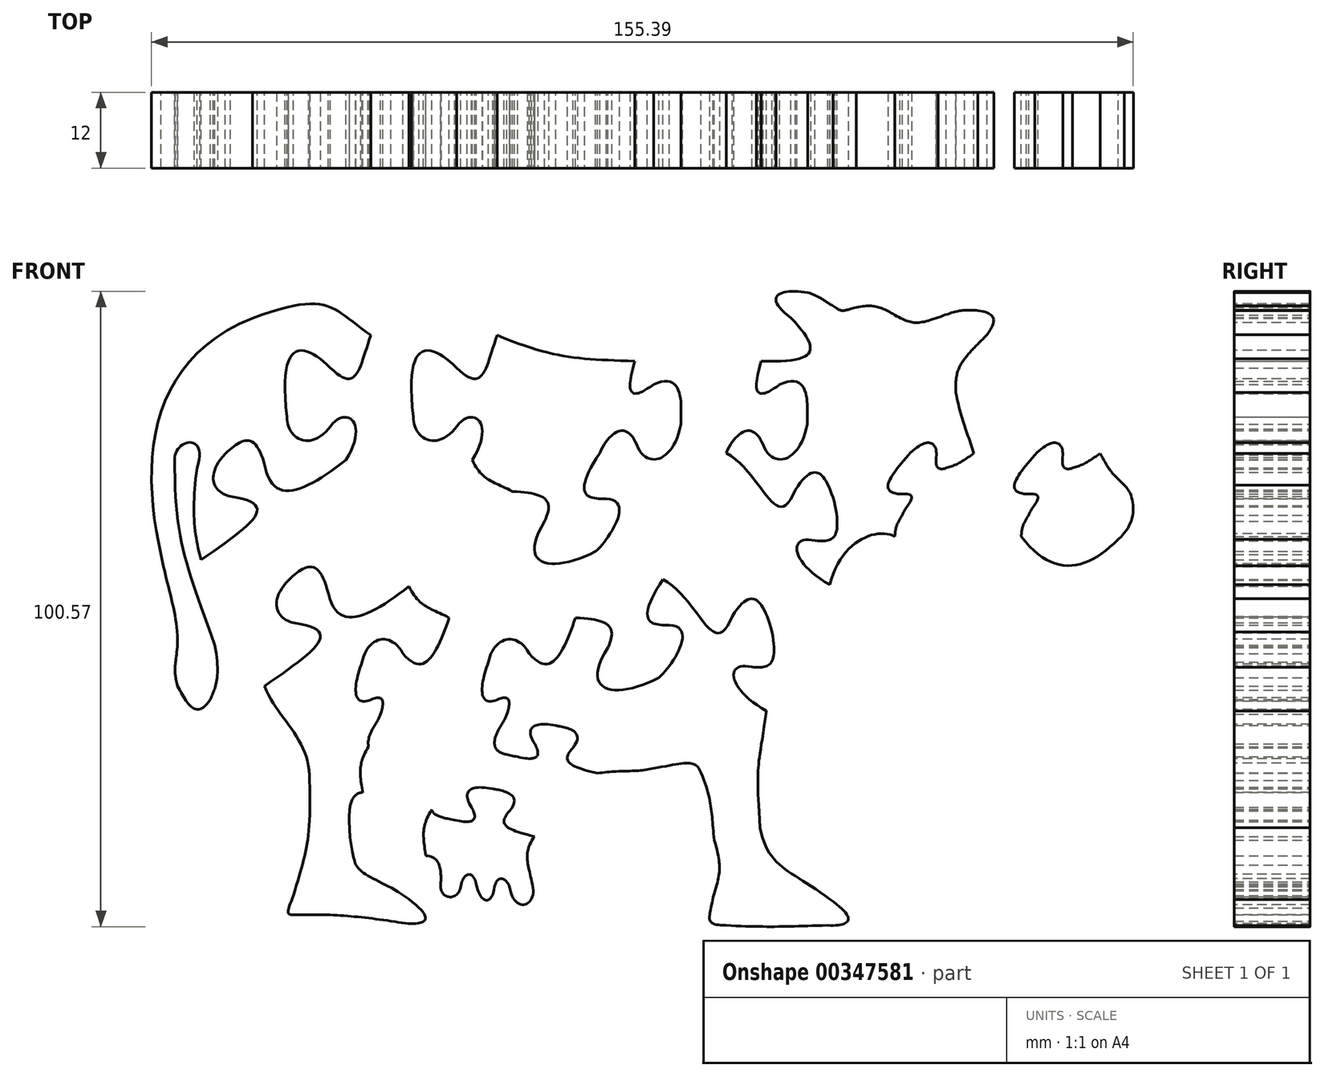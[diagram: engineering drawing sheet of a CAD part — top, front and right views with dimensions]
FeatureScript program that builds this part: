
annotation { "Feature Type Name" : "Feature", "Feature Type Description" : "" }
export const myFeature = defineFeature(function(context is Context, id is Id, definition is map)
    precondition{}
    {
        {
            var Q0;
            Q0=qCreatedBy(makeId("Front.planeOp"),FACE);
            var sketch = newSketch(context, id + "F0", { "sketchPlane" : qUnion([Q0])});
            skFitSpline(sketch, "E0", {"points": [v(-32.6, 40.87) * mm, v(-13.83, 38.18) * mm], "startDerivative": vector(36.75, 13.6) * mm, "endDerivative": vector(18.9, -13.17) * mm});
            skFitSpline(sketch, "E1", {"points": [v(-13.83, 38.18) * mm, v(7.96, 34.07) * mm], "startDerivative": vector(27.03, -11.28) * mm, "endDerivative": vector(27.04, -1.05) * mm});
            skFitSpline(sketch, "E2", {"points": [v(7.96, 34.07) * mm, v(12.64, 40.93) * mm], "startDerivative": vector(26.9, -0.75) * mm, "endDerivative": vector(-14.95, 15.64) * mm});
            skFitSpline(sketch, "E3", {"points": [v(12.64, 40.93) * mm, v(15.32, 44.94) * mm], "startDerivative": vector(-14.2, 10.76) * mm, "endDerivative": vector(12.86, -2.14) * mm});
            skFitSpline(sketch, "E4", {"points": [v(15.32, 44.94) * mm, v(19.28, 42.85) * mm], "startDerivative": vector(6.61, -2.14) * mm, "endDerivative": vector(3.96, -2.08) * mm});
            skFitSpline(sketch, "E5", {"points": [v(19.28, 42.85) * mm, v(22.97, 42.59) * mm], "startDerivative": vector(5.1, -3.48) * mm, "endDerivative": vector(6.7, 1.6) * mm});
            skFitSpline(sketch, "E6", {"points": [v(22.97, 42.59) * mm, v(29.1, 41.4) * mm], "startDerivative": vector(8.42, 1.81) * mm, "endDerivative": vector(6.88, -3.85) * mm});
            skFitSpline(sketch, "E7", {"points": [v(29.1, 41.4) * mm, v(35.97, 41) * mm], "startDerivative": vector(7.85, -4.56) * mm, "endDerivative": vector(10.17, 3.54) * mm});
            skFitSpline(sketch, "E8", {"points": [v(35.97, 41) * mm, v(42.23, 42.1) * mm], "startDerivative": vector(9.41, 3.73) * mm, "endDerivative": vector(6.05, -0.42) * mm});
            skFitSpline(sketch, "E9", {"points": [v(42.23, 42.1) * mm, v(43.66, 38.26) * mm], "startDerivative": vector(10.46, -1.27) * mm, "endDerivative": vector(-3.88, -5.31) * mm});
            skFitSpline(sketch, "E10", {"points": [v(43.66, 38.26) * mm, v(40.14, 34.44) * mm], "startDerivative": vector(-3.52, -3.83) * mm, "endDerivative": vector(-2.7, -3.83) * mm});
            skFitSpline(sketch, "E11", {"points": [v(40.14, 34.44) * mm, v(38.76, 29.15) * mm], "startDerivative": vector(-2.71, -3.71) * mm, "endDerivative": vector(0.5, -8.98) * mm});
            skFitSpline(sketch, "E12", {"points": [v(38.76, 29.15) * mm, v(41.59, 19.46) * mm], "startDerivative": vector(1.98, -11.9) * mm, "endDerivative": vector(2.83, -9.68) * mm});
            skFitSpline(sketch, "E13", {"points": [v(41.59, 19.46) * mm, v(45.4, 14.49) * mm], "startDerivative": vector(5.55, -9.57) * mm, "endDerivative": vector(7.68, -7.6) * mm});
            skFitSpline(sketch, "E14", {"points": [v(45.4, 14.49) * mm, v(44.48, 5.88) * mm], "startDerivative": vector(3.5, -2.88) * mm, "endDerivative": vector(-11.58, -10.62) * mm});
            skFitSpline(sketch, "E15", {"points": [v(44.48, 5.88) * mm, v(29.1, 6.32) * mm], "startDerivative": vector(-15.47, -15.15) * mm, "endDerivative": vector(-15.4, 19.97) * mm});
            skFitSpline(sketch, "E16", {"points": [v(29.1, 6.32) * mm, v(18.77, -1.27) * mm], "startDerivative": vector(-8.35, 4.52) * mm, "endDerivative": vector(-5.56, -21.35) * mm});
            skFitSpline(sketch, "E17", {"points": [v(18.77, -1.27) * mm, v(17.74, -19.77) * mm], "startDerivative": vector(-4.61, -31.74) * mm, "endDerivative": vector(1.77, -31.83) * mm});
            skFitSpline(sketch, "E18", {"points": [v(17.74, -19.77) * mm, v(28.86, -31.14) * mm], "startDerivative": vector(3.79, -19.45) * mm, "endDerivative": vector(18.45, -14.1) * mm});
            skFitSpline(sketch, "E19", {"points": [v(28.86, -31.14) * mm, v(28.48, -35.22) * mm], "startDerivative": vector(13.52, -9.38) * mm, "endDerivative": vector(-10.73, 0.53) * mm});
            skFitSpline(sketch, "E20", {"points": [v(28.48, -35.22) * mm, v(12.33, -35.22) * mm], "startDerivative": vector(-20.18, -0.53) * mm, "endDerivative": vector(-19.76, 1.06) * mm});
            skFitSpline(sketch, "E21", {"points": [v(12.33, -35.22) * mm, v(10.35, -30.72) * mm], "startDerivative": vector(-10.25, 0.1) * mm, "endDerivative": vector(2.08, 10.8) * mm});
            skFitSpline(sketch, "E22", {"points": [v(10.35, -30.72) * mm, v(10.53, -21.73) * mm], "startDerivative": vector(3.7, 12.56) * mm, "endDerivative": vector(-3.53, 13.37) * mm});
            skFitSpline(sketch, "E23", {"points": [v(10.53, -21.73) * mm, v(8.41, -11.1) * mm], "startDerivative": vector(-1.53, 11.85) * mm, "endDerivative": vector(-5.71, 13.17) * mm});
            skFitSpline(sketch, "E24", {"points": [v(8.41, -11.1) * mm, v(0.13, -10.53) * mm], "startDerivative": vector(-2.39, 7.03) * mm, "endDerivative": vector(-17.65, -3.15) * mm});
            skFitSpline(sketch, "E25", {"points": [v(0.13, -10.53) * mm, v(-7.94, -11.16) * mm], "startDerivative": vector(-7.33, -1.3) * mm, "endDerivative": vector(-8.76, -1.49) * mm});
            skFitSpline(sketch, "E26", {"points": [v(-7.94, -11.16) * mm, v(-8.37, -18.33) * mm], "startDerivative": vector(-5.4, -8) * mm, "endDerivative": vector(2.18, -10.22) * mm});
            skFitSpline(sketch, "E27", {"points": [v(-8.37, -18.33) * mm, v(-11.76, -19.7) * mm], "startDerivative": vector(3.57, -11.42) * mm, "endDerivative": vector(-2.55, 11.27) * mm});
            skFitSpline(sketch, "E28", {"points": [v(-11.76, -19.7) * mm, v(-14.33, -19.53) * mm], "startDerivative": vector(-0.7, 5.71) * mm, "endDerivative": vector(-1.2, -8.34) * mm});
            skFitSpline(sketch, "E29", {"points": [v(-14.33, -19.53) * mm, v(-17.13, -18.86) * mm], "startDerivative": vector(-1.33, -7.58) * mm, "endDerivative": vector(-2.02, 8.78) * mm});
            skFitSpline(sketch, "E30", {"points": [v(-17.13, -18.86) * mm, v(-19.64, -19.13) * mm], "startDerivative": vector(-1.26, 7.33) * mm, "endDerivative": vector(-1.26, -7.26) * mm});
            skFitSpline(sketch, "E31", {"points": [v(-19.64, -19.13) * mm, v(-22.77, -18.65) * mm], "startDerivative": vector(-1.14, -7.01) * mm, "endDerivative": vector(0.76, 7.77) * mm});
            skFitSpline(sketch, "E32", {"points": [v(-22.77, -18.65) * mm, v(-25.14, -14.2) * mm], "startDerivative": vector(0.17, 5.69) * mm, "endDerivative": vector(-7.4, 0.25) * mm});
            skFitSpline(sketch, "E33", {"points": [v(-25.14, -14.2) * mm, v(-27.2, -16.85) * mm], "startDerivative": vector(-2.65, 0.13) * mm, "endDerivative": vector(-0.7, -5.81) * mm});
            skFitSpline(sketch, "E34", {"points": [v(-27.2, -16.85) * mm, v(-26.2, -25.68) * mm], "startDerivative": vector(-0.66, -10.53) * mm, "endDerivative": vector(2.25, -5.66) * mm});
            skFitSpline(sketch, "E35", {"points": [v(-26.2, -25.68) * mm, v(-16.2, -32.46) * mm], "startDerivative": vector(3.35, -6.53) * mm, "endDerivative": vector(12.53, -11.9) * mm});
            skFitSpline(sketch, "E36", {"points": [v(-16.2, -32.46) * mm, v(-20.65, -34.54) * mm], "startDerivative": vector(7.09, -7.02) * mm, "endDerivative": vector(-14.53, 2.78) * mm});
            skFitSpline(sketch, "E37", {"points": [v(-20.65, -34.54) * mm, v(-33.65, -33.53) * mm], "startDerivative": vector(-14.02, 2) * mm, "endDerivative": vector(-13.12, -0.16) * mm});
            skFitSpline(sketch, "E38", {"points": [v(-33.65, -33.53) * mm, v(-36.08, -30.5) * mm], "startDerivative": vector(-10.83, 0.29) * mm, "endDerivative": vector(4.67, 11.56) * mm});
            skFitSpline(sketch, "E39", {"points": [v(-36.08, -30.5) * mm, v(-33.54, -12.28) * mm], "startDerivative": vector(5.42, 19.32) * mm, "endDerivative": vector(-1.06, 29.55) * mm});
            skFitSpline(sketch, "E40", {"points": [v(-33.54, -12.28) * mm, v(-40.69, 2.62) * mm], "startDerivative": vector(0.43, 19.64) * mm, "endDerivative": vector(-7.01, 16.68) * mm});
            skFitSpline(sketch, "E41", {"points": [v(-40.69, 2.62) * mm, v(-41.37, 17.2) * mm], "startDerivative": vector(-3.27, 10.8) * mm, "endDerivative": vector(2.72, 20.38) * mm});
            skFitSpline(sketch, "E42", {"points": [v(-41.37, 17.2) * mm, v(-44.89, 18.82) * mm], "startDerivative": vector(5.43, 16.82) * mm, "endDerivative": vector(-0.75, -8.92) * mm});
            skFitSpline(sketch, "E43", {"points": [v(-44.89, 18.82) * mm, v(-38.54, -10.85) * mm], "startDerivative": vector(-0.13, -40.71) * mm, "endDerivative": vector(13.7, -39.02) * mm});
            skFitSpline(sketch, "E44", {"points": [v(-38.54, -10.85) * mm, v(-39.25, -19.44) * mm], "startDerivative": vector(3, -16.76) * mm, "endDerivative": vector(-2.25, -5.7) * mm});
            skFitSpline(sketch, "E45", {"points": [v(-39.25, -19.44) * mm, v(-44.45, -17.33) * mm], "startDerivative": vector(-6.61, -10.52) * mm, "endDerivative": vector(-4.06, 7.81) * mm});
            skFitSpline(sketch, "E46", {"points": [v(-44.45, -17.33) * mm, v(-44.45, -11.08) * mm], "startDerivative": vector(-1.78, 6.83) * mm, "endDerivative": vector(1.3, 10.73) * mm});
            skFitSpline(sketch, "E47", {"points": [v(-44.45, -11.08) * mm, v(-47.05, 3.47) * mm], "startDerivative": vector(0.82, 13.69) * mm, "endDerivative": vector(-2.6, 14.55) * mm});
            skFitSpline(sketch, "E48", {"points": [v(-47.05, 3.47) * mm, v(-32.6, 40.87) * mm], "startDerivative": vector(-10.08, 44.17) * mm, "endDerivative": vector(49.75, 19.85) * mm});
            skFitSpline(sketch, "E49", {"points": [v(41.59, 19.46) * mm, v(37.19, 17.16) * mm], "startDerivative": vector(-4.06, -2.71) * mm, "endDerivative": vector(-5.53, -1.33) * mm});
            skFitSpline(sketch, "E50", {"points": [v(37.19, 17.16) * mm, v(35.63, 18.84) * mm], "startDerivative": vector(-5.3, -1.86) * mm, "endDerivative": vector(0.1, 2.23) * mm});
            skFitSpline(sketch, "E51", {"points": [v(35.63, 18.84) * mm, v(31.25, 19.22) * mm], "startDerivative": vector(1.07, 8.26) * mm, "endDerivative": vector(-7.96, -8.78) * mm});
            skFitSpline(sketch, "E52", {"points": [v(31.25, 19.22) * mm, v(29.94, 13.04) * mm], "startDerivative": vector(-9.12, -10.49) * mm, "endDerivative": vector(10.63, -0.9) * mm});
            skFitSpline(sketch, "E53", {"points": [v(29.94, 13.04) * mm, v(30.28, 9.72) * mm], "startDerivative": vector(10.67, 0.86) * mm, "endDerivative": vector(-1.97, -5.18) * mm});
            skFitSpline(sketch, "E54", {"points": [v(30.28, 9.72) * mm, v(29.1, 6.32) * mm], "startDerivative": vector(-2.26, -3.8) * mm, "endDerivative": vector(-0.4, -5.34) * mm});
            skFitSpline(sketch, "E55", {"points": [v(7.96, 34.07) * mm, v(10.9, 30.4) * mm], "startDerivative": vector(-4.41, -14.48) * mm, "endDerivative": vector(11.87, 8.86) * mm});
            skFitSpline(sketch, "E56", {"points": [v(10.9, 30.4) * mm, v(15.25, 24.09) * mm], "startDerivative": vector(15.92, 7.51) * mm, "endDerivative": vector(0.3, -5.56) * mm});
            skFitSpline(sketch, "E57", {"points": [v(15.25, 24.09) * mm, v(8.23, 20.9) * mm], "startDerivative": vector(-3.37, -17.8) * mm, "endDerivative": vector(-4.82, 12.33) * mm});
            skFitSpline(sketch, "E58", {"points": [v(8.23, 20.9) * mm, v(2.4, 19.57) * mm], "startDerivative": vector(-4.36, 10.8) * mm, "endDerivative": vector(-5.18, -11.37) * mm});
            skFitSpline(sketch, "E59", {"points": [v(2.4, 19.57) * mm, v(3.4, 12.31) * mm], "startDerivative": vector(-13.4, -20.52) * mm, "endDerivative": vector(9.29, 0.18) * mm});
            skFitSpline(sketch, "E60", {"points": [v(3.4, 12.31) * mm, v(1.74, 3.97) * mm], "startDerivative": vector(14.65, -0.9) * mm, "endDerivative": vector(-4.5, -3.56) * mm});
            skFitSpline(sketch, "E61", {"points": [v(1.74, 3.97) * mm, v(-6.34, 8.72) * mm], "startDerivative": vector(-20.38, -10.46) * mm, "endDerivative": vector(13.7, 22.03) * mm});
            skFitSpline(sketch, "E62", {"points": [v(-6.34, 8.72) * mm, v(-11.44, 13.47) * mm], "startDerivative": vector(4.68, 10.06) * mm, "endDerivative": vector(-16.37, 0.75) * mm});
            skFitSpline(sketch, "E63", {"points": [v(-11.44, 13.47) * mm, v(-17.8, 18.44) * mm], "startDerivative": vector(-9.28, 4.84) * mm, "endDerivative": vector(-4.5, 9.76) * mm});
            skFitSpline(sketch, "E64", {"points": [v(-17.8, 18.44) * mm, v(-20.57, 23.33) * mm], "startDerivative": vector(11.36, 18.08) * mm, "endDerivative": vector(-8.08, -12.25) * mm});
            skFitSpline(sketch, "E65", {"points": [v(-20.57, 23.33) * mm, v(-27.1, 25.27) * mm], "startDerivative": vector(-9.47, -11) * mm, "endDerivative": vector(0.63, 9.35) * mm});
            skFitSpline(sketch, "E66", {"points": [v(-27.1, 25.27) * mm, v(-20.26, 33.03) * mm], "startDerivative": vector(-4.88, 38.3) * mm, "endDerivative": vector(12.38, -12.5) * mm});
            skFitSpline(sketch, "E67", {"points": [v(-20.26, 33.03) * mm, v(-13.83, 38.18) * mm], "startDerivative": vector(13.04, -12.48) * mm, "endDerivative": vector(5.84, 15.94) * mm});
            skFitSpline(sketch, "E68", {"points": [v(-7.94, -11.16) * mm, v(-11.86, -7.1) * mm], "startDerivative": vector(-13.99, 3.34) * mm, "endDerivative": vector(5.95, 6.48) * mm});
            skFitSpline(sketch, "E69", {"points": [v(-11.86, -7.1) * mm, v(-14.55, -3.6) * mm], "startDerivative": vector(7.33, 9.14) * mm, "endDerivative": vector(-1.91, 0.64) * mm});
            skFitSpline(sketch, "E70", {"points": [v(-14.55, -3.6) * mm, v(-17.9, -6.53) * mm], "startDerivative": vector(-10.85, 2.1) * mm, "endDerivative": vector(5.03, -7.74) * mm});
            skFitSpline(sketch, "E71", {"points": [v(-17.9, -6.53) * mm, v(-20.6, -8.56) * mm], "startDerivative": vector(3.08, -5.7) * mm, "endDerivative": vector(-9.76, 2.25) * mm});
            skFitSpline(sketch, "E72", {"points": [v(-20.6, -8.56) * mm, v(-24.22, -6.91) * mm], "startDerivative": vector(-7.06, 1.36) * mm, "endDerivative": vector(-1.03, 2.81) * mm});
            skFitSpline(sketch, "E73", {"points": [v(-24.22, -6.91) * mm, v(-22.31, -1.8) * mm], "startDerivative": vector(-1.02, 5.64) * mm, "endDerivative": vector(1.9, 5.12) * mm});
            skFitSpline(sketch, "E74", {"points": [v(-22.31, -1.8) * mm, v(-24.14, 0.37) * mm], "startDerivative": vector(2.3, 6.78) * mm, "endDerivative": vector(-6.53, -3.42) * mm});
            skFitSpline(sketch, "E75", {"points": [v(-24.14, 0.37) * mm, v(-25.24, 6.44) * mm], "startDerivative": vector(-8.55, -2.7) * mm, "endDerivative": vector(3.83, 10.3) * mm});
            skFitSpline(sketch, "E76", {"points": [v(-25.24, 6.44) * mm, v(-18.76, 7.82) * mm], "startDerivative": vector(2.03, 11.27) * mm, "endDerivative": vector(6.37, -11.47) * mm});
            skFitSpline(sketch, "E77", {"points": [v(-18.76, 7.82) * mm, v(-11.44, 13.47) * mm], "startDerivative": vector(10.6, -13.14) * mm, "endDerivative": vector(5.51, 15.54) * mm});
            skFitSpline(sketch, "E78", {"points": [v(-40.69, 2.62) * mm, v(-36.07, 12.65) * mm], "startDerivative": vector(23.02, 16.29) * mm, "endDerivative": vector(-25.09, 3.46) * mm});
            skFitSpline(sketch, "E79", {"points": [v(-36.07, 12.65) * mm, v(-36.88, 19.44) * mm], "startDerivative": vector(-7.54, 1.86) * mm, "endDerivative": vector(10.2, 10.94) * mm});
            skFitSpline(sketch, "E80", {"points": [v(-36.88, 19.44) * mm, v(-30.54, 17.2) * mm], "startDerivative": vector(7.65, 7.33) * mm, "endDerivative": vector(4.36, -18.27) * mm});
            skFitSpline(sketch, "E81", {"points": [v(-30.54, 17.2) * mm, v(-17.8, 18.44) * mm], "startDerivative": vector(4.46, -18.66) * mm, "endDerivative": vector(18.62, 14.4) * mm});
            skFitSpline(sketch, "E82", {"points": [v(2.4, 19.57) * mm, v(13.37, 13.7) * mm], "startDerivative": vector(18.08, -10.61) * mm, "endDerivative": vector(9.29, 21.97) * mm});
            skFitSpline(sketch, "E83", {"points": [v(13.37, 13.7) * mm, v(19.66, 11.23) * mm], "startDerivative": vector(9.1, 14.66) * mm, "endDerivative": vector(4.25, -15.93) * mm});
            skFitSpline(sketch, "E84", {"points": [v(19.66, 11.23) * mm, v(16.46, 5.67) * mm], "startDerivative": vector(2.91, -16.16) * mm, "endDerivative": vector(-8.4, 0.9) * mm});
            skFitSpline(sketch, "E85", {"points": [v(16.46, 5.67) * mm, v(18.77, -1.27) * mm], "startDerivative": vector(-13.11, 3.12) * mm, "endDerivative": vector(18.6, -10.26) * mm});
            skFitSpline(sketch, "E86", {"points": [v(-24.22, -6.91) * mm, v(-25.14, -14.2) * mm], "startDerivative": vector(-5.08, -8.43) * mm, "endDerivative": vector(1.43, -9.42) * mm});
            skSolve(sketch);
        }
        {
            var Q0;
            Q0=makeQuery(id+"F0.imprint","IMPRINT",FACE,{"disambiguationData":[TD([[makeQuery(id+"F0.imprint","IMPRINT",EDGE,{"derivedFrom":sQuery(id+"F0.wireOp",EDGE,"E0")}),-1.0]])]});
            extrude(context, id + "F1", {"entities" : qUnion([Q0]), "depth" : 12 * mm});
        }
        {
            var Q0;
            Q0=makeQuery(id+"F1.opExtrude","SWEPT_BODY",BODY,{"disambiguationData":[OSD([sQuery(id+"F0.wireOp",EDGE,"E0"),sQuery(id+"F0.wireOp",EDGE,"E41"),sQuery(id+"F0.wireOp",EDGE,"E42"),sQuery(id+"F0.wireOp",EDGE,"E43"),sQuery(id+"F0.wireOp",EDGE,"E44"),sQuery(id+"F0.wireOp",EDGE,"E45"),sQuery(id+"F0.wireOp",EDGE,"E46"),sQuery(id+"F0.wireOp",EDGE,"E47"),sQuery(id+"F0.wireOp",EDGE,"E48"),sQuery(id+"F0.wireOp",EDGE,"E64"),sQuery(id+"F0.wireOp",EDGE,"E65"),sQuery(id+"F0.wireOp",EDGE,"E66"),sQuery(id+"F0.wireOp",EDGE,"E67"),sQuery(id+"F0.wireOp",EDGE,"E78"),sQuery(id+"F0.wireOp",EDGE,"E79"),sQuery(id+"F0.wireOp",EDGE,"E80"),sQuery(id+"F0.wireOp",EDGE,"E81")])]});
            transform(context, id + "F2", {"entities" : qUnion([Q0]), "transformType" : TransformType.TRANSLATION_3D, "dx" : -20 * mm, "dy" : 0 * mm, "dz" : -90 * mm, "makeCopy" : false});
        }
        {
            var Q0;
            Q0=makeQuery(id+"F0.imprint","IMPRINT",FACE,{"disambiguationData":[TD([[makeQuery(id+"F0.imprint","IMPRINT",EDGE,{"derivedFrom":sQuery(id+"F0.wireOp",EDGE,"E1")}),-1.0]])]});
            extrude(context, id + "F3", {"entities" : qUnion([Q0]), "depth" : 12 * mm});
        }
        {
            var Q0;
            Q0=makeQuery(id+"F3.opExtrude","SWEPT_BODY",BODY,{"disambiguationData":[OSD([sQuery(id+"F0.wireOp",EDGE,"E1"),sQuery(id+"F0.wireOp",EDGE,"E55"),sQuery(id+"F0.wireOp",EDGE,"E56"),sQuery(id+"F0.wireOp",EDGE,"E57"),sQuery(id+"F0.wireOp",EDGE,"E58"),sQuery(id+"F0.wireOp",EDGE,"E59"),sQuery(id+"F0.wireOp",EDGE,"E60"),sQuery(id+"F0.wireOp",EDGE,"E61"),sQuery(id+"F0.wireOp",EDGE,"E62"),sQuery(id+"F0.wireOp",EDGE,"E63"),sQuery(id+"F0.wireOp",EDGE,"E64"),sQuery(id+"F0.wireOp",EDGE,"E65"),sQuery(id+"F0.wireOp",EDGE,"E66"),sQuery(id+"F0.wireOp",EDGE,"E67")])]});
            transform(context, id + "F4", {"entities" : qUnion([Q0]), "transformType" : TransformType.TRANSLATION_3D, "dx" : 0 * mm, "dy" : 0 * mm, "dz" : -90 * mm, "makeCopy" : false});
        }
        {
            var Q0;
            Q0=makeQuery(id+"F0.imprint","IMPRINT",FACE,{"disambiguationData":[TD([[makeQuery(id+"F0.imprint","IMPRINT",EDGE,{"derivedFrom":sQuery(id+"F0.wireOp",EDGE,"E2")}),-1.0]])]});
            extrude(context, id + "F5", {"entities" : qUnion([Q0]), "depth" : 12 * mm});
        }
        {
            var Q0;
            Q0=makeQuery(id+"F5.opExtrude","SWEPT_BODY",BODY,{"disambiguationData":[OSD([sQuery(id+"F0.wireOp",EDGE,"E2"),sQuery(id+"F0.wireOp",EDGE,"E3"),sQuery(id+"F0.wireOp",EDGE,"E4"),sQuery(id+"F0.wireOp",EDGE,"E5"),sQuery(id+"F0.wireOp",EDGE,"E6"),sQuery(id+"F0.wireOp",EDGE,"E7"),sQuery(id+"F0.wireOp",EDGE,"E8"),sQuery(id+"F0.wireOp",EDGE,"E9"),sQuery(id+"F0.wireOp",EDGE,"E10"),sQuery(id+"F0.wireOp",EDGE,"E11"),sQuery(id+"F0.wireOp",EDGE,"E12"),sQuery(id+"F0.wireOp",EDGE,"E16"),sQuery(id+"F0.wireOp",EDGE,"E49"),sQuery(id+"F0.wireOp",EDGE,"E50"),sQuery(id+"F0.wireOp",EDGE,"E51"),sQuery(id+"F0.wireOp",EDGE,"E52"),sQuery(id+"F0.wireOp",EDGE,"E53"),sQuery(id+"F0.wireOp",EDGE,"E54"),sQuery(id+"F0.wireOp",EDGE,"E55"),sQuery(id+"F0.wireOp",EDGE,"E56"),sQuery(id+"F0.wireOp",EDGE,"E57"),sQuery(id+"F0.wireOp",EDGE,"E58"),sQuery(id+"F0.wireOp",EDGE,"E82"),sQuery(id+"F0.wireOp",EDGE,"E83"),sQuery(id+"F0.wireOp",EDGE,"E84"),sQuery(id+"F0.wireOp",EDGE,"E85")])]});
            transform(context, id + "F6", {"entities" : qUnion([Q0]), "transformType" : TransformType.TRANSLATION_3D, "dx" : 20 * mm, "dy" : 0 * mm, "dz" : -90 * mm, "makeCopy" : false});
        }
        {
            var Q0;
            Q0=makeQuery(id+"F0.imprint","IMPRINT",FACE,{"disambiguationData":[TD([[makeQuery(id+"F0.imprint","IMPRINT",EDGE,{"derivedFrom":sQuery(id+"F0.wireOp",EDGE,"E13")}),-1.0]])]});
            extrude(context, id + "F7", {"entities" : qUnion([Q0]), "depth" : 12 * mm});
        }
        {
            var Q0;
            Q0=makeQuery(id+"F7.opExtrude","SWEPT_BODY",BODY,{"disambiguationData":[OSD([sQuery(id+"F0.wireOp",EDGE,"E13"),sQuery(id+"F0.wireOp",EDGE,"E14"),sQuery(id+"F0.wireOp",EDGE,"E15"),sQuery(id+"F0.wireOp",EDGE,"E49"),sQuery(id+"F0.wireOp",EDGE,"E50"),sQuery(id+"F0.wireOp",EDGE,"E51"),sQuery(id+"F0.wireOp",EDGE,"E52"),sQuery(id+"F0.wireOp",EDGE,"E53"),sQuery(id+"F0.wireOp",EDGE,"E54")])]});
            transform(context, id + "F8", {"entities" : qUnion([Q0]), "transformType" : TransformType.TRANSLATION_3D, "dx" : 40 * mm, "dy" : 0 * mm, "dz" : -90 * mm, "makeCopy" : false});
        }
        {
            var Q0;
            Q0=makeQuery(id+"F0.imprint","IMPRINT",FACE,{"disambiguationData":[TD([[makeQuery(id+"F0.imprint","IMPRINT",EDGE,{"derivedFrom":sQuery(id+"F0.wireOp",EDGE,"E33")}),-1.0]])]});
            extrude(context, id + "F9", {"entities" : qUnion([Q0]), "depth" : 12 * mm});
        }
        {
            var Q0;
            Q0=makeQuery(id+"F9.opExtrude","SWEPT_BODY",BODY,{"disambiguationData":[OSD([sQuery(id+"F0.wireOp",EDGE,"E33"),sQuery(id+"F0.wireOp",EDGE,"E34"),sQuery(id+"F0.wireOp",EDGE,"E35"),sQuery(id+"F0.wireOp",EDGE,"E36"),sQuery(id+"F0.wireOp",EDGE,"E37"),sQuery(id+"F0.wireOp",EDGE,"E38"),sQuery(id+"F0.wireOp",EDGE,"E39"),sQuery(id+"F0.wireOp",EDGE,"E40"),sQuery(id+"F0.wireOp",EDGE,"E63"),sQuery(id+"F0.wireOp",EDGE,"E73"),sQuery(id+"F0.wireOp",EDGE,"E74"),sQuery(id+"F0.wireOp",EDGE,"E75"),sQuery(id+"F0.wireOp",EDGE,"E76"),sQuery(id+"F0.wireOp",EDGE,"E77"),sQuery(id+"F0.wireOp",EDGE,"E78"),sQuery(id+"F0.wireOp",EDGE,"E79"),sQuery(id+"F0.wireOp",EDGE,"E80"),sQuery(id+"F0.wireOp",EDGE,"E81"),sQuery(id+"F0.wireOp",EDGE,"E86")])]});
            transform(context, id + "F10", {"entities" : qUnion([Q0]), "transformType" : TransformType.TRANSLATION_3D, "dx" : -10 * mm, "dy" : 0 * mm, "dz" : -110 * mm, "makeCopy" : false});
        }
        {
            var Q0;
            Q0=makeQuery(id+"F0.imprint","IMPRINT",FACE,{"disambiguationData":[TD([[makeQuery(id+"F0.imprint","IMPRINT",EDGE,{"derivedFrom":sQuery(id+"F0.wireOp",EDGE,"E17")}),-1.0]])]});
            extrude(context, id + "F11", {"entities" : qUnion([Q0]), "depth" : 12 * mm});
        }
        {
            var Q0;
            Q0=makeQuery(id+"F11.opExtrude","SWEPT_BODY",BODY,{"disambiguationData":[OSD([sQuery(id+"F0.wireOp",EDGE,"E17"),sQuery(id+"F0.wireOp",EDGE,"E18"),sQuery(id+"F0.wireOp",EDGE,"E19"),sQuery(id+"F0.wireOp",EDGE,"E20"),sQuery(id+"F0.wireOp",EDGE,"E21"),sQuery(id+"F0.wireOp",EDGE,"E22"),sQuery(id+"F0.wireOp",EDGE,"E23"),sQuery(id+"F0.wireOp",EDGE,"E24"),sQuery(id+"F0.wireOp",EDGE,"E25"),sQuery(id+"F0.wireOp",EDGE,"E59"),sQuery(id+"F0.wireOp",EDGE,"E60"),sQuery(id+"F0.wireOp",EDGE,"E61"),sQuery(id+"F0.wireOp",EDGE,"E62"),sQuery(id+"F0.wireOp",EDGE,"E68"),sQuery(id+"F0.wireOp",EDGE,"E69"),sQuery(id+"F0.wireOp",EDGE,"E70"),sQuery(id+"F0.wireOp",EDGE,"E71"),sQuery(id+"F0.wireOp",EDGE,"E72"),sQuery(id+"F0.wireOp",EDGE,"E73"),sQuery(id+"F0.wireOp",EDGE,"E74"),sQuery(id+"F0.wireOp",EDGE,"E75"),sQuery(id+"F0.wireOp",EDGE,"E76"),sQuery(id+"F0.wireOp",EDGE,"E77"),sQuery(id+"F0.wireOp",EDGE,"E82"),sQuery(id+"F0.wireOp",EDGE,"E83"),sQuery(id+"F0.wireOp",EDGE,"E84"),sQuery(id+"F0.wireOp",EDGE,"E85")])]});
            transform(context, id + "F12", {"entities" : qUnion([Q0]), "transformType" : TransformType.TRANSLATION_3D, "dx" : 10 * mm, "dy" : 0 * mm, "dz" : -110 * mm, "makeCopy" : false});
        }
        {
            var Q0;
            Q0=makeQuery(id+"F0.imprint","IMPRINT",FACE,{"disambiguationData":[TD([[makeQuery(id+"F0.imprint","IMPRINT",EDGE,{"derivedFrom":sQuery(id+"F0.wireOp",EDGE,"E26")}),-1.0]])]});
            extrude(context, id + "F13", {"entities" : qUnion([Q0]), "depth" : 12 * mm});
        }
        {
            var Q0;
            Q0=makeQuery(id+"F13.opExtrude","SWEPT_BODY",BODY,{"disambiguationData":[OSD([sQuery(id+"F0.wireOp",EDGE,"E26"),sQuery(id+"F0.wireOp",EDGE,"E27"),sQuery(id+"F0.wireOp",EDGE,"E28"),sQuery(id+"F0.wireOp",EDGE,"E29"),sQuery(id+"F0.wireOp",EDGE,"E30"),sQuery(id+"F0.wireOp",EDGE,"E31"),sQuery(id+"F0.wireOp",EDGE,"E32"),sQuery(id+"F0.wireOp",EDGE,"E68"),sQuery(id+"F0.wireOp",EDGE,"E69"),sQuery(id+"F0.wireOp",EDGE,"E70"),sQuery(id+"F0.wireOp",EDGE,"E71"),sQuery(id+"F0.wireOp",EDGE,"E72"),sQuery(id+"F0.wireOp",EDGE,"E86")])]});
            transform(context, id + "F14", {"entities" : qUnion([Q0]), "transformType" : TransformType.TRANSLATION_3D, "dx" : 0 * mm, "dy" : 0 * mm, "dz" : -120 * mm, "makeCopy" : false});
        }
    });
